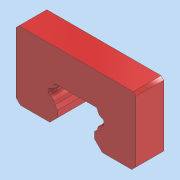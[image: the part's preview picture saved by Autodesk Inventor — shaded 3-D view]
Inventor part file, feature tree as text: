
AUTODESK INVENTOR PART (.ipt)
format: ipt  version: 2021 (Build 250183000, 183)  size: 154,624 bytes
history: native  units: mm
features: extrude x3, sketch x2, projected_geometry x1
ambient origin geometry x8: Origin, YZ Plane, XZ Plane, XY Plane, X Axis, Y Axis, Z Axis, Center Point
bodies: Solid1 (feature_tree)
feature tree (6):
  sketch  "Sketch1"  dims[d0=10.0mm d1=0.0mm d2=2.1mm d3=0.0mm]
  extrude  "Extrusion1"  Depth=2.1mm TaperAngle=0.0deg
  extrude  "Extrusion2"  [1 undecoded]
  extrude  "Extrusion3"  [1 undecoded]
  sketch  "Sketch2"  dims[d4=4.0mm d5=0.0mm]
  projected_geometry  "Projected Loop1"
note: 2 required parameter values undecoded (feature->parameter linkage not recoverable at this tier; creation-order binding heuristic only, values carry confidence <= 0.55)
